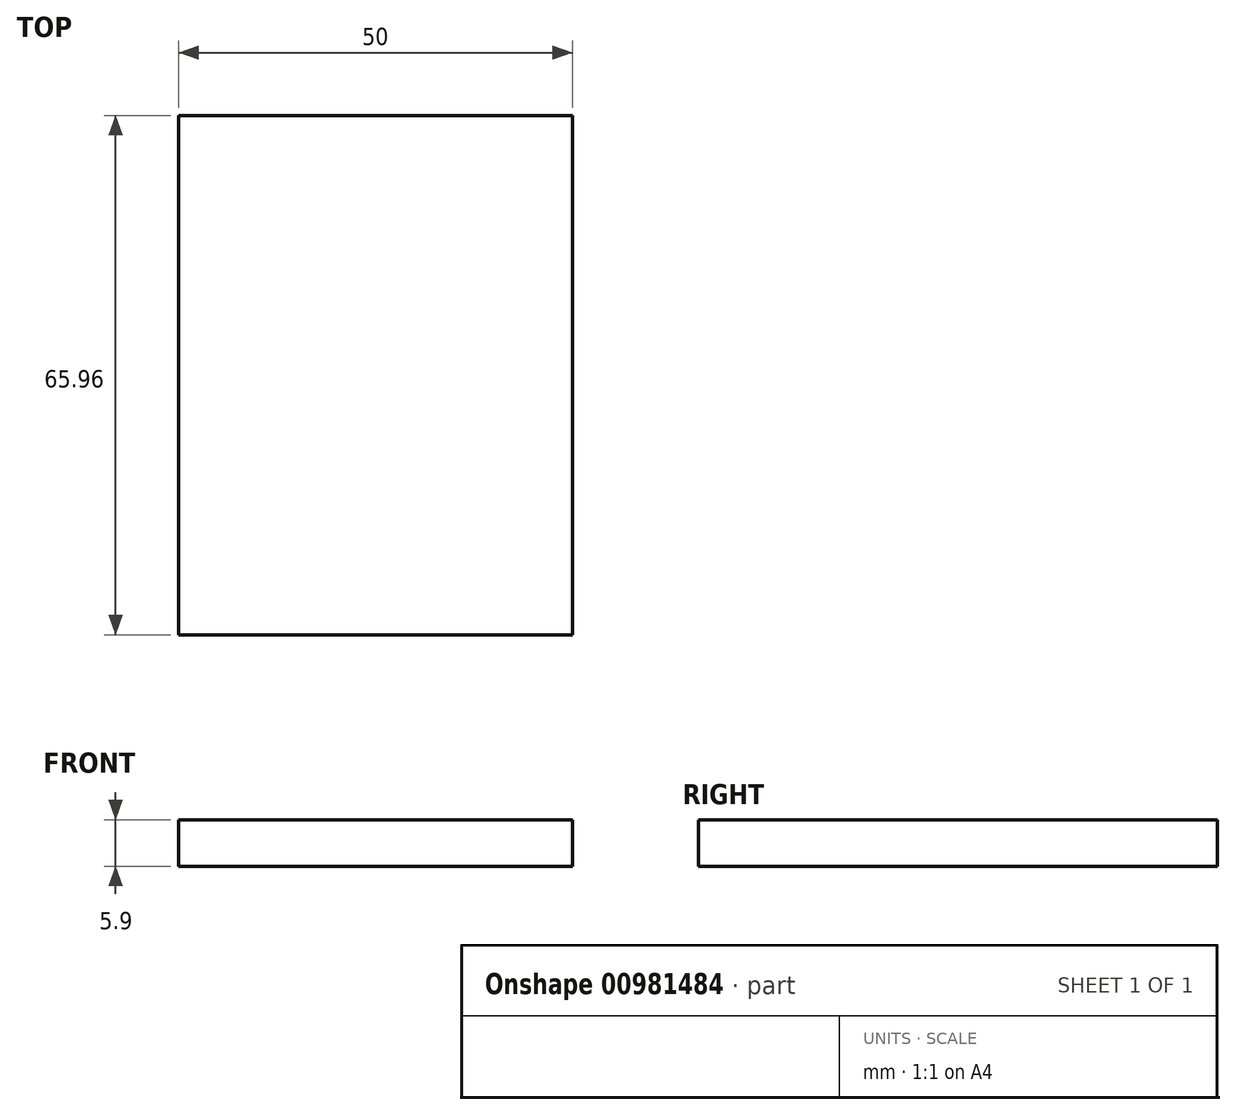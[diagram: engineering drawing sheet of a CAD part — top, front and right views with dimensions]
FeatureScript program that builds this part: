
annotation { "Feature Type Name" : "Feature", "Feature Type Description" : "" }
export const myFeature = defineFeature(function(context is Context, id is Id, definition is map)
    precondition{}
    {
        {
            var Q0;
            Q0=qCreatedBy(makeId("Top.planeOp"),FACE);
            var sketch = newSketch(context, id + "F0", { "sketchPlane" : qUnion([Q0])});
            skLineSegment(sketch, "E0.bottom", {"start": v(-33.23, 25.96) * mm, "end": v(16.77, 25.96) * mm});
            skLineSegment(sketch, "E0.top", {"start": v(-33.23, -40) * mm, "end": v(16.77, -40) * mm});
            skLineSegment(sketch, "E0.left", {"start": v(-33.23, 25.96) * mm, "end": v(-33.23, -40) * mm});
            skLineSegment(sketch, "E0.right", {"start": v(16.77, 25.96) * mm, "end": v(16.77, -40) * mm});
            skSolve(sketch);
        }
        {
            var Q0;
            Q0=makeQuery(id+"F0.imprint","IMPRINT",FACE,{"disambiguationData":[TD([[makeQuery(id+"F0.imprint","IMPRINT",EDGE,{"derivedFrom":sQuery(id+"F0.wireOp",EDGE,"E0.bottom")}),-1.0]])]});
            extrude(context, id + "F1", {"entities" : qUnion([Q0]), "depth" : 5.9 * mm, "offsetDistance" : 25 * mm});
        }
    });
